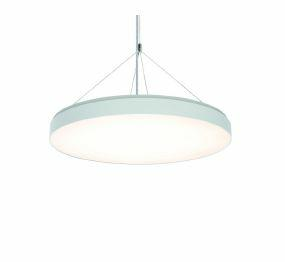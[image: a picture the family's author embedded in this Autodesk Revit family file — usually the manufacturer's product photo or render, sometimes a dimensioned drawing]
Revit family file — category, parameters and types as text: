
# Revit family: spectral_stora_stora-rp-led_4300_840_os_ddf9
name_source: partatom
category: Lighting Fixtures
revit_build: Autodesk Revit 2016 (Build: 20150220_1215(x64)
units: mm (PartAtom-declared; Revit-internal decimal feet)

## family parameters
Cut with Voids When Loaded = No
Host = Face
Light Source = No
Part Type = Normal
Room Calculation Point = No
Round Connector Dimension = Use Diameter
Shared = No

## types (1)
- SPECTRAL STORA (1 x )
    Apparent Load = 0 VA
    CIE Flux Codes = 48 78 95 100 100
    Control Gear = Electronic transformer
    Default Elevation = 1800 mm
    Description = SPC0620009
STORA pendant LED luminaire

Design:
Round luminaire element with an opal acrylic panel mounted in a profile frame made of power-coated aluminium. The frame is fastened on the powdercoated steel body using a bayonet catch with spring clip. The luminaire is suspended by four trapezoidal wire pendants with ceiling fixture and transparent connecting cable with round ceiling junction box. The cable length can be adjusted at the ceiling junction box, the steel wire can be steplessly height adjusted. The steel body houses the electrical components and electronic ballast. The LED module is formed as a round LED flat board and can be removed for mounting or exchange using a keyhole screw connection. Plug-in electrical connection of the LED flat board. The luminaire is configured with heatresistant wiring. Homogeneous illumination of the light surface. Light colour 4000 K (840). Also in a dimmable version.
Protection rating IP20, safety class I.

Colour:
Frame – similar to RAL 9016 white silk matt
    Height = 76 mm
    Lamp = 1 x
    Lamp count = 1
    Length = 420 mm
    Luminous efficacy = 0 lm/W
    Manufacturer = Ridi
    ModVariant = No
    Model = STORA-RP-LED 4300/840 OS
    Number of Poles = 1
    OnlyDefault = Yes
    Power Factor = 1
    Product Name = SPECTRAL STORA
    Product group = Ceiling / wall-mounted luminaires
    ProductGroupID = 30
    Protection Class = Protection class
    Protection Degree = Degree of protection
    RlxData = <blob elided: 7037 chars, md5=7d21f7ec>
    Socket = socket
    Standby Power = 0 W
    System Light Flux = 0 lm
    System Power = 0 W
    Type Image = stora-rp.jpg
    URL = http://reluxnet.relux.com
    VarID = 1
    Voltage = 0 V
    Weight = 0.00 kg
    Width = 0 mm  [stored 0 ft]

note: [stored X ft] marks values corroborated as IEEE doubles in the binary element streams (Revit-internal decimal feet)

## geometry (parser evidence)
native form markers: Sweep x9
no freeform markers — native parametric forms only
